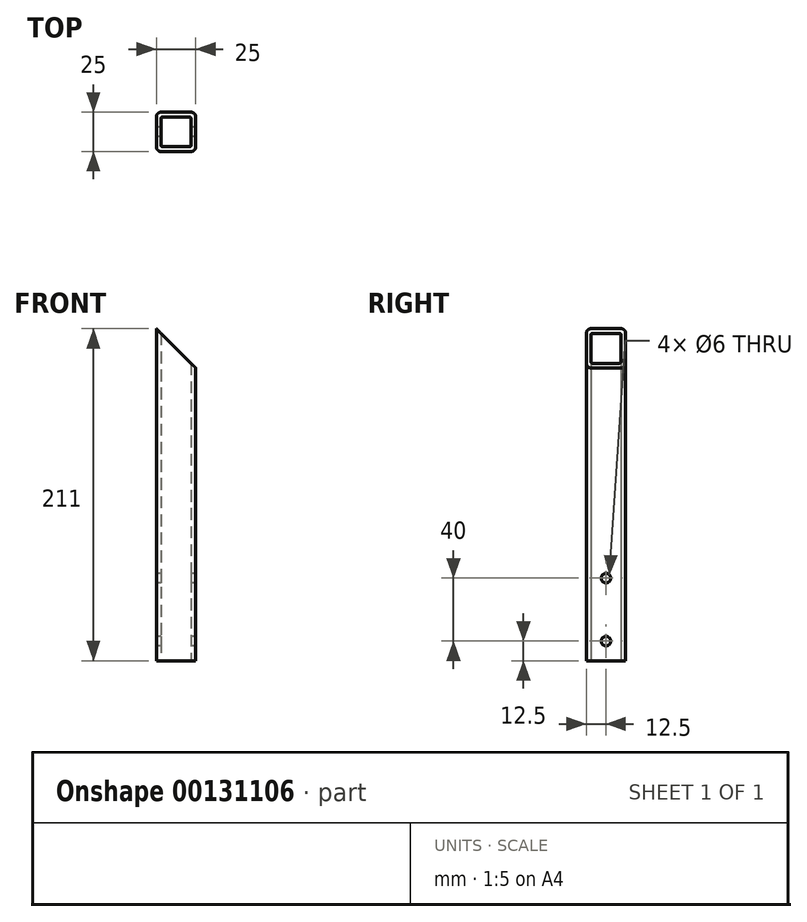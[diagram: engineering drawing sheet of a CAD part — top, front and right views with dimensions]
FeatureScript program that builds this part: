
annotation { "Feature Type Name" : "Feature", "Feature Type Description" : "" }
export const myFeature = defineFeature(function(context is Context, id is Id, definition is map)
    precondition{}
    {
        {
            var Q0;
            Q0=qCreatedBy(makeId("Top.planeOp"),FACE);
            var sketch = newSketch(context, id + "F0", { "sketchPlane" : qUnion([Q0])});
            skLineSegment(sketch, "E0.bottom", {"start": v(12.5, -12.5) * mm, "end": v(-12.5, -12.5) * mm});
            skLineSegment(sketch, "E0.top", {"start": v(12.5, 12.5) * mm, "end": v(-12.5, 12.5) * mm});
            skLineSegment(sketch, "E0.left", {"start": v(12.5, -12.5) * mm, "end": v(12.5, 12.5) * mm});
            skLineSegment(sketch, "E0.right", {"start": v(-12.5, -12.5) * mm, "end": v(-12.5, 12.5) * mm});
            skPoint(sketch, "E0.middle", {"position": v(0, 0) * mm});
            skLineSegment(sketch, "E1.bottom", {"start": v(9.5, -9.5) * mm, "end": v(-9.5, -9.5) * mm});
            skLineSegment(sketch, "E1.top", {"start": v(9.5, 9.5) * mm, "end": v(-9.5, 9.5) * mm});
            skLineSegment(sketch, "E1.left", {"start": v(9.5, -9.5) * mm, "end": v(9.5, 9.5) * mm});
            skLineSegment(sketch, "E1.right", {"start": v(-9.5, -9.5) * mm, "end": v(-9.5, 9.5) * mm});
            skSolve(sketch);
        }
        {
            var Q0;
            Q0=makeQuery(id+"F0.imprint","IMPRINT",FACE,{"disambiguationData":[TD([[makeQuery(id+"F0.imprint","IMPRINT",EDGE,{"derivedFrom":sQuery(id+"F0.wireOp",EDGE,"E0.bottom")}),-1.0]])]});
            extrude(context, id + "F1", {"entities" : qUnion([Q0]), "depth" : 211 * mm});
        }
        {
            var Q0;
            Q0=makeQuery(id+"F1.opExtrude","SWEPT_EDGE",EDGE,{"disambiguationData":[OSD([sQuery(id+"F0.wireOp",EDGE,"E1.bottom"),sQuery(id+"F0.wireOp",EDGE,"E1.right")])]});
            var Q1;
            Q1=makeQuery(id+"F1.opExtrude","SWEPT_EDGE",EDGE,{"disambiguationData":[OSD([sQuery(id+"F0.wireOp",EDGE,"E1.top"),sQuery(id+"F0.wireOp",EDGE,"E1.right")])]});
            var Q2;
            Q2=makeQuery(id+"F1.opExtrude","SWEPT_EDGE",EDGE,{"disambiguationData":[OSD([sQuery(id+"F0.wireOp",EDGE,"E1.top"),sQuery(id+"F0.wireOp",EDGE,"E1.left")])]});
            var Q3;
            Q3=makeQuery(id+"F1.opExtrude","SWEPT_EDGE",EDGE,{"disambiguationData":[OSD([sQuery(id+"F0.wireOp",EDGE,"E1.bottom"),sQuery(id+"F0.wireOp",EDGE,"E1.left")])]});
            fillet(context, id + "F2", {"entities" : qUnion([Q0, Q1, Q2, Q3]), "radius" : 1 * mm, "tangentPropagation" : true, "allowEdgeOverflow" : false});
        }
        {
            var Q0;
            Q0=makeQuery(id+"F1.opExtrude","SWEPT_EDGE",EDGE,{"disambiguationData":[OSD([sQuery(id+"F0.wireOp",EDGE,"E0.top"),sQuery(id+"F0.wireOp",EDGE,"E0.right")])]});
            var Q1;
            Q1=makeQuery(id+"F1.opExtrude","SWEPT_EDGE",EDGE,{"disambiguationData":[OSD([sQuery(id+"F0.wireOp",EDGE,"E0.bottom"),sQuery(id+"F0.wireOp",EDGE,"E0.right")])]});
            var Q2;
            Q2=makeQuery(id+"F1.opExtrude","SWEPT_EDGE",EDGE,{"disambiguationData":[OSD([sQuery(id+"F0.wireOp",EDGE,"E0.top"),sQuery(id+"F0.wireOp",EDGE,"E0.left")])]});
            var Q3;
            Q3=makeQuery(id+"F1.opExtrude","SWEPT_EDGE",EDGE,{"disambiguationData":[OSD([sQuery(id+"F0.wireOp",EDGE,"E0.bottom"),sQuery(id+"F0.wireOp",EDGE,"E0.left")])]});
            fillet(context, id + "F3", {"entities" : qUnion([Q0, Q1, Q2, Q3]), "radius" : 3 * mm, "tangentPropagation" : true, "allowEdgeOverflow" : false});
        }
        {
            var Q0;
            Q0=makeQuery(id+"F1.opExtrude","SWEPT_FACE",FACE,{"disambiguationData":[OSD([sQuery(id+"F0.wireOp",EDGE,"E0.bottom")])]});
            var sketch = newSketch(context, id + "F4", { "sketchPlane" : qUnion([Q0])});
            skLineSegment(sketch, "E2", {"start": v(-12.5, 211) * mm, "end": v(12.5, 186) * mm});
            skPoint(sketch, "E2.startSnap0", {"position": v(0, 211) * mm});
            skLineSegment(sketch, "E3", {"start": v(12.5, 186) * mm, "end": v(12.5, 211) * mm});
            skLineSegment(sketch, "E4", {"start": v(-12.5, 211) * mm, "end": v(12.5, 211) * mm});
            skSolve(sketch);
        }
        {
            var Q0;
            {var subQ0=sQuery(id+"F4.wireOp",EDGE,"E2");var subQ1=sQuery(id+"F0.wireOp",EDGE,"E0.bottom");var subQ2=makeQuery(id+"F1.opExtrude","SWEPT_FACE",FACE,{"disambiguationData":[OSD([subQ1])]});var subQ3=makeQuery(id+"F3.opFillet","BLEND_EDGE",EDGE,{"blendedFrom":[makeQuery(id+"F1.opExtrude","SWEPT_EDGE",EDGE,{"disambiguationData":[OSD([subQ1,sQuery(id+"F0.wireOp",EDGE,"E0.right")])]}),subQ2],"blendedInto":[subQ2]});var subQ4=makeQuery(id+"F4.imprint","INTERSECT",VERTEX,{"derivedFrom":[subQ3,subQ0]});Q0=makeQuery(id+"F4.imprint","IMPRINT",FACE,{"disambiguationData":[TD([[makeQuery(id+"F4.imprint","IMPRINT",EDGE,{"disambiguationData":[TD([[subQ4,-1.0]])],"derivedFrom":subQ0}),1.0]])]});}
            var Q1;
            {var subQ0=sQuery(id+"F4.wireOp",EDGE,"E4");var subQ1=sQuery(id+"F4.wireOp",EDGE,"E2");var subQ2=makeQuery(id+"F4.imprint","INTERSECT",VERTEX,{"derivedFrom":[subQ1,subQ0]});Q1=makeQuery(id+"F4.imprint","IMPRINT",FACE,{"disambiguationData":[TD([[makeQuery(id+"F4.imprint","IMPRINT",EDGE,{"disambiguationData":[TD([[subQ2,-1.0]])],"derivedFrom":subQ1}),1.0]])]});}
            var Q2;
            {var subQ0=sQuery(id+"F4.wireOp",EDGE,"E3");Q2=makeQuery(id+"F4.imprint","IMPRINT",FACE,{"disambiguationData":[TD([[makeQuery(id+"F4.imprint","IMPRINT",EDGE,{"derivedFrom":subQ0}),1.0]])]});}
            extrude(context, id + "F5", {"entities" : qUnion([Q0, Q1, Q2]), "operationType" : NewBodyOperationType.REMOVE, "endBound" : BoundingType.THROUGH_ALL, "oppositeDirection" : true, "depth" : 25 * mm});
        }
        {
            var Q0;
            Q0=makeQuery(id+"F1.opExtrude","SWEPT_FACE",FACE,{"disambiguationData":[OSD([sQuery(id+"F0.wireOp",EDGE,"E0.right")])]});
            var sketch = newSketch(context, id + "F6", { "sketchPlane" : qUnion([Q0])});
            skPoint(sketch, "E5", {"position": v(0, 12.5) * mm});
            skPoint(sketch, "E6", {"position": v(0, 52.5) * mm});
            skSolve(sketch);
        }
        {
            var Q0;
            Q0=sQuery(id+"F6.wireOp",VERTEX,"E5");
            var Q1;
            Q1=sQuery(id+"F6.wireOp",VERTEX,"E6");
            var Q2;
            Q2=makeQuery(id+"F1.opExtrude","SWEPT_BODY",BODY,{"disambiguationData":[OSD([sQuery(id+"F0.wireOp",EDGE,"E0.bottom"),sQuery(id+"F0.wireOp",EDGE,"E0.top"),sQuery(id+"F0.wireOp",EDGE,"E0.left"),sQuery(id+"F0.wireOp",EDGE,"E0.right"),sQuery(id+"F0.wireOp",EDGE,"E1.bottom"),sQuery(id+"F0.wireOp",EDGE,"E1.top"),sQuery(id+"F0.wireOp",EDGE,"E1.left"),sQuery(id+"F0.wireOp",EDGE,"E1.right")])]});
            hole(context, id + "F7", {"style" : HoleStyle.SIMPLE, "endStyle" : HoleEndStyle.THROUGH, "holeDiameter" : 6 * mm, "locations" : qUnion([Q0, Q1]), "scope" : qUnion([Q2]), "isTappedThrough" : true});
        }
    });
